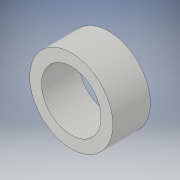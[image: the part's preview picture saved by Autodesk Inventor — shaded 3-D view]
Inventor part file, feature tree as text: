
AUTODESK INVENTOR PART (.ipt)
format: ipt  version: 2019 (Build 230136000, 136)  size: 102,912 bytes
history: native  units: mm
features: extrude x2, sketch x2
ambient origin geometry x8: Origin, YZ Plane, XZ Plane, XY Plane, X Axis, Y Axis, Z Axis, Center Point
bodies: Solid1 (feature_tree)
feature tree (4):
  extrude  "Extrusion1"  Depth=180.0mm TaperAngle=0.0deg
  extrude  "Extrusion2"  Depth=180.0mm TaperAngle=0.0deg
  sketch  "Sketch1"  dims[d0=400.0mm d1=180.0mm d2=0.0mm]
  sketch  "Sketch2"  dims[d3=286.0mm d4=180.0mm d5=0.0mm]
